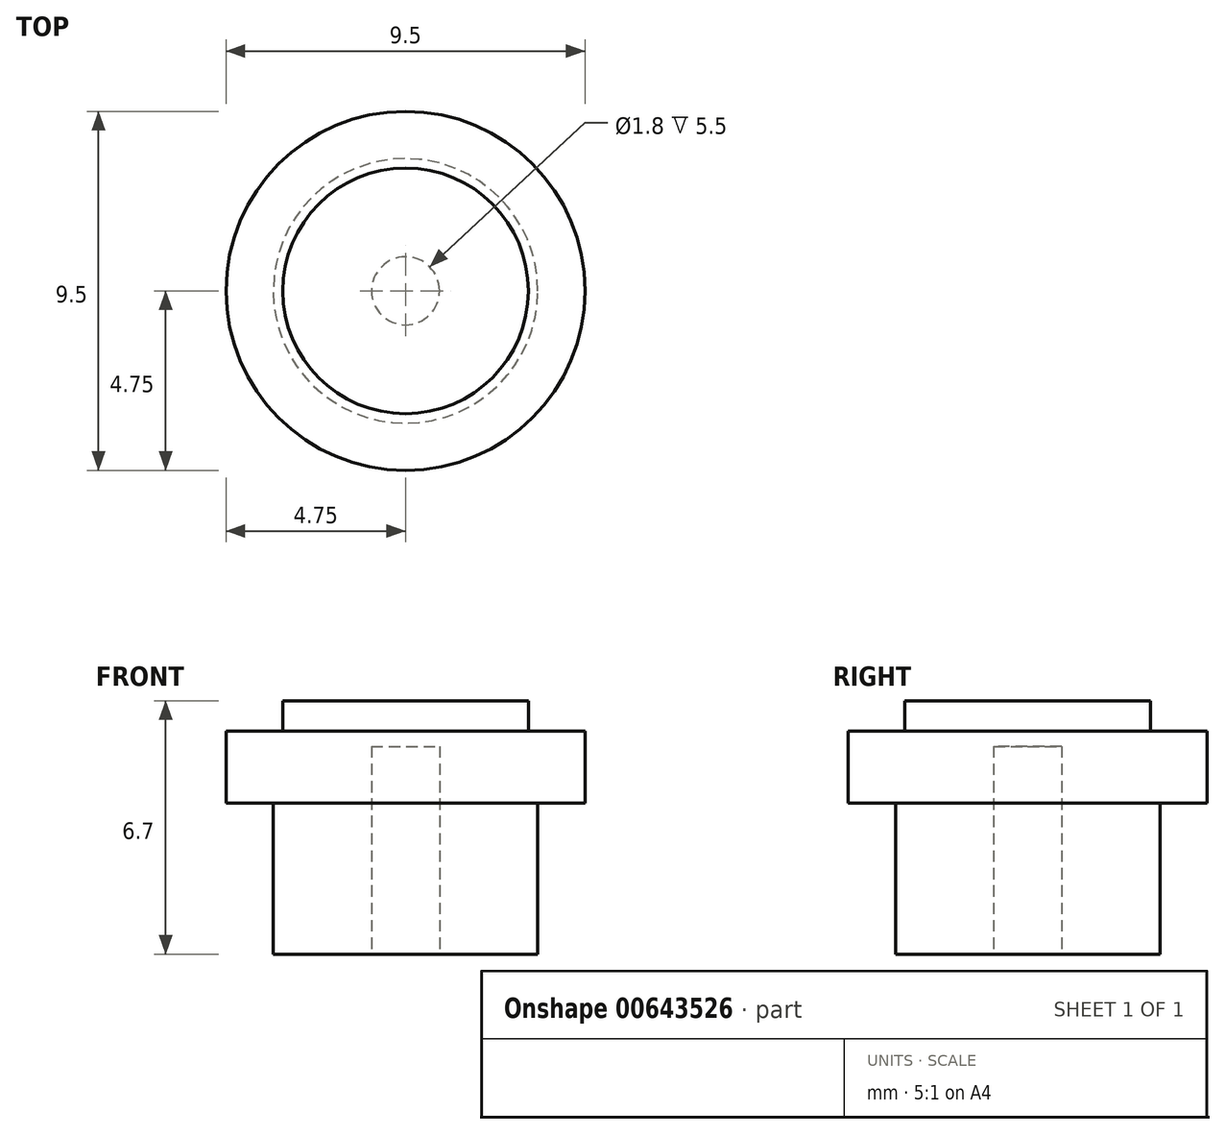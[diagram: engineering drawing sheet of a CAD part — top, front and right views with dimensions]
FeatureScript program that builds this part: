
annotation { "Feature Type Name" : "Feature", "Feature Type Description" : "" }
export const myFeature = defineFeature(function(context is Context, id is Id, definition is map)
    precondition{}
    {
        {
            var Q0;
            Q0=qCreatedBy(makeId("Top.planeOp"),FACE);
            var sketch = newSketch(context, id + "F0", { "sketchPlane" : qUnion([Q0])});
            skCircle(sketch, "E0", {"center": v(0, 0) * mm, "radius": 3.5 * mm});
            skSolve(sketch);
        }
        {
            var Q0;
            Q0 = qSketchRegion(id + "F0", true);
            extrude(context, id + "F1", {"entities" : qUnion([Q0]), "depth" : 4 * mm, "offsetDistance" : 25 * mm});
        }
        {
            var Q0;
            Q0=makeQuery(id+"F1.opExtrude","CAP_FACE",FACE,{"disambiguationData":[OSD([sQuery(id+"F0.wireOp",EDGE,"E0")])],"isStart":false});
            var sketch = newSketch(context, id + "F2", { "sketchPlane" : qUnion([Q0])});
            skCircle(sketch, "E1", {"center": v(0, 0) * mm, "radius": 4.75 * mm});
            skSolve(sketch);
        }
        {
            var Q0;
            Q0=makeQuery(id+"F2.imprint","IMPRINT",FACE,{"disambiguationData":[TD([[makeQuery(id+"F2.imprint","IMPRINT",EDGE,{"derivedFrom":sQuery(id+"F2.wireOp",EDGE,"E1")}),1.0]])]});
            var Q1;
            Q1=makeQuery(id+"F2.imprint","IMPRINT",FACE,{"disambiguationData":[TD([[makeQuery(id+"F2.imprint","IMPRINT",EDGE,{"derivedFrom":makeQuery(id+"F1.opExtrude","CAP_EDGE",EDGE,{"disambiguationData":[OSD([sQuery(id+"F0.wireOp",EDGE,"E0")])],"isStart":false})}),1.0]])]});
            extrude(context, id + "F3", {"entities" : qUnion([Q0, Q1]), "operationType" : NewBodyOperationType.ADD, "depth" : 1.9 * mm, "offsetDistance" : 25 * mm});
        }
        {
            var Q0;
            Q0=makeQuery(id+"F3.opExtrude","CAP_FACE",FACE,{"disambiguationData":[OSD([sQuery(id+"F2.wireOp",EDGE,"E1")])],"isStart":false});
            var sketch = newSketch(context, id + "F4", { "sketchPlane" : qUnion([Q0])});
            skCircle(sketch, "E2", {"center": v(0, 0) * mm, "radius": 3.25 * mm});
            skSolve(sketch);
        }
        {
            var Q0;
            Q0=makeQuery(id+"F4.imprint","IMPRINT",FACE,{"disambiguationData":[TD([[makeQuery(id+"F4.imprint","IMPRINT",EDGE,{"derivedFrom":sQuery(id+"F4.wireOp",EDGE,"E2")}),1.0]])]});
            extrude(context, id + "F5", {"entities" : qUnion([Q0]), "operationType" : NewBodyOperationType.ADD, "depth" : 0.8 * mm, "offsetDistance" : 25 * mm});
        }
        {
            var Q0;
            Q0=makeQuery(id+"F1.opExtrude","CAP_FACE",FACE,{"disambiguationData":[OSD([sQuery(id+"F0.wireOp",EDGE,"E0")])],"isStart":true});
            var sketch = newSketch(context, id + "F6", { "sketchPlane" : qUnion([Q0])});
            skCircle(sketch, "E3", {"center": v(0, 0) * mm, "radius": 0.9 * mm});
            skSolve(sketch);
        }
        {
            var Q0;
            Q0=makeQuery(id+"F6.imprint","IMPRINT",FACE,{"disambiguationData":[TD([[makeQuery(id+"F6.imprint","IMPRINT",EDGE,{"derivedFrom":sQuery(id+"F6.wireOp",EDGE,"E3")}),1.0]])]});
            extrude(context, id + "F7", {"entities" : qUnion([Q0]), "operationType" : NewBodyOperationType.REMOVE, "oppositeDirection" : true, "depth" : 5.5 * mm, "offsetDistance" : 25 * mm});
        }
    });
